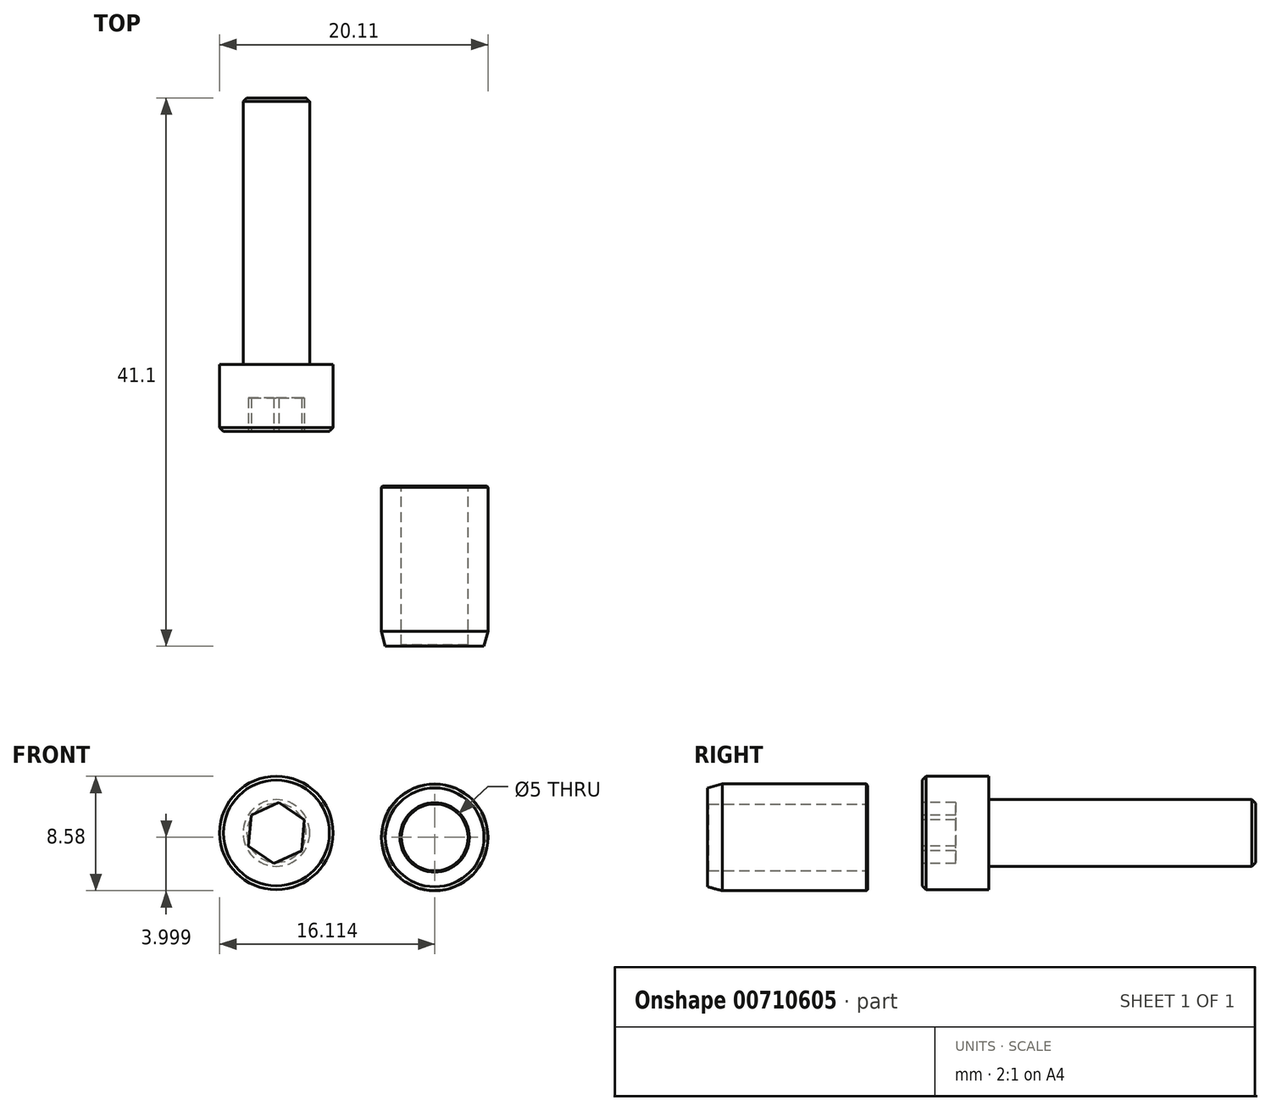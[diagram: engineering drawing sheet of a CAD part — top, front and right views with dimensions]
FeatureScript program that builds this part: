
annotation { "Feature Type Name" : "Feature", "Feature Type Description" : "" }
export const myFeature = defineFeature(function(context is Context, id is Id, definition is map)
    precondition{}
    {
        {
            var Q0;
            Q0=qCreatedBy(makeId("Top.planeOp"),FACE);
            var sketch = newSketch(context, id + "F0", { "sketchPlane" : qUnion([Q0])});
            skLineSegment(sketch, "E0.bottom", {"start": v(3.05, 9.1) * mm, "end": v(4.8, 9.1) * mm});
            skLineSegment(sketch, "E0.top", {"start": v(3.33, 4.1) * mm, "end": v(7.3, 4.1) * mm});
            skLineSegment(sketch, "E0.left", {"start": v(3.05, 9.1) * mm, "end": v(3.05, 4.38) * mm});
            skLineSegment(sketch, "E0.right", {"start": v(7.3, 9.1) * mm, "end": v(7.3, 4.1) * mm});
            skLineSegment(sketch, "E1.top", {"start": v(7.3, 29.1) * mm, "end": v(5.08, 29.1) * mm});
            skLineSegment(sketch, "E1.left", {"start": v(7.3, 9.1) * mm, "end": v(7.3, 29.1) * mm});
            skLineSegment(sketch, "E1.right", {"start": v(4.8, 9.1) * mm, "end": v(4.8, 28.82) * mm});
            skLineSegment(sketch, "E2", {"start": v(3.05, 4.38) * mm, "end": v(3.33, 4.1) * mm});
            skLineSegment(sketch, "E3", {"start": v(4.8, 28.82) * mm, "end": v(5.08, 29.1) * mm});
            skSolve(sketch);
        }
        {
            var Q0;
            Q0 = qSketchRegion(id + "F0", true);
            var Q1;
            Q1=sQuery(id+"F0.wireOp",EDGE,"E1.left");
            revolve(context, id + "F1", {"surfaceOperationType" : NewSurfaceOperationType.NEW, "entities" : qUnion([Q0]), "axis" : qUnion([Q1]), "revolveType" : RevolveType.FULL});
        }
        {
            var Q0;
            Q0=makeQuery(id+"F1.opRevolve","SWEPT_FACE",FACE,{"disambiguationData":[OSD([sQuery(id+"F0.wireOp",EDGE,"E0.top")])]});
            var sketch = newSketch(context, id + "F2", { "sketchPlane" : qUnion([Q0])});
            skCircle(sketch, "E4.cCircle", {"center": v(7.3, 0) * mm, "radius": 2 * mm, "construction": true});
            skLineSegment(sketch, "E4.0", {"start": v(7.5, 2.3) * mm, "end": v(9.4, 0.98) * mm});
            skLineSegment(sketch, "E4.1", {"start": v(9.4, 0.98) * mm, "end": v(9.2, -1.32) * mm});
            skLineSegment(sketch, "E4.2", {"start": v(9.2, -1.32) * mm, "end": v(7.1, -2.3) * mm});
            skLineSegment(sketch, "E4.3", {"start": v(7.1, -2.3) * mm, "end": v(5.2, -0.98) * mm});
            skLineSegment(sketch, "E4.4", {"start": v(5.2, -0.98) * mm, "end": v(5.4, 1.32) * mm});
            skLineSegment(sketch, "E4.5", {"start": v(5.4, 1.32) * mm, "end": v(7.5, 2.3) * mm});
            skPoint(sketch, "E4.0.midPoint", {"position": v(8.44, 1.64) * mm});
            skSolve(sketch);
        }
        {
            var Q0;
            Q0 = qSketchRegion(id + "F2", true);
            extrude(context, id + "F3", {"entities" : qUnion([Q0]), "operationType" : NewBodyOperationType.REMOVE, "oppositeDirection" : true, "depth" : 2.5 * mm, "offsetDistance" : 25 * mm});
        }
        {
            var Q0;
            Q0=qCreatedBy(makeId("Front.planeOp"),FACE);
            var sketch = newSketch(context, id + "F4", { "sketchPlane" : qUnion([Q0])});
            skCircle(sketch, "E5", {"center": v(19.16, -0.33) * mm, "radius": 4 * mm});
            skCircle(sketch, "E6", {"center": v(19.16, -0.33) * mm, "radius": 2.5 * mm});
            skSolve(sketch);
        }
        {
            var Q0;
            Q0 = qSketchRegion(id + "F4", true);
            extrude(context, id + "F5", {"entities" : qUnion([Q0]), "depth" : 12 * mm, "offsetDistance" : 25 * mm});
        }
        {
            var Q0;
            Q0=makeQuery(id+"F5.opExtrude","CAP_EDGE",EDGE,{"disambiguationData":[OSD([sQuery(id+"F4.wireOp",EDGE,"E5")])],"isStart":false});
            chamfer(context, id + "F6", {"entities" : qUnion([Q0]), "chamferType" : ChamferType.OFFSET_ANGLE, "width" : 0.3 * mm, "oppositeDirection" : false, "angle" : 75 * degree});
        }
        {
            var Q0;
            Q0=makeQuery(id+"F5.opExtrude","CAP_EDGE",EDGE,{"disambiguationData":[OSD([sQuery(id+"F4.wireOp",EDGE,"E5")])],"isStart":true});
            var Q1;
            Q1=makeQuery(id+"F5.opExtrude","CAP_EDGE",EDGE,{"disambiguationData":[OSD([sQuery(id+"F4.wireOp",EDGE,"E6")])],"isStart":true});
            var Q2;
            Q2=makeQuery(id+"F5.opExtrude","CAP_EDGE",EDGE,{"disambiguationData":[OSD([sQuery(id+"F4.wireOp",EDGE,"E6")])],"isStart":false});
            chamfer(context, id + "F7", {"entities" : qUnion([Q0, Q1, Q2]), "width" : 0.1 * mm, "tangentPropagation" : true});
        }
    });
